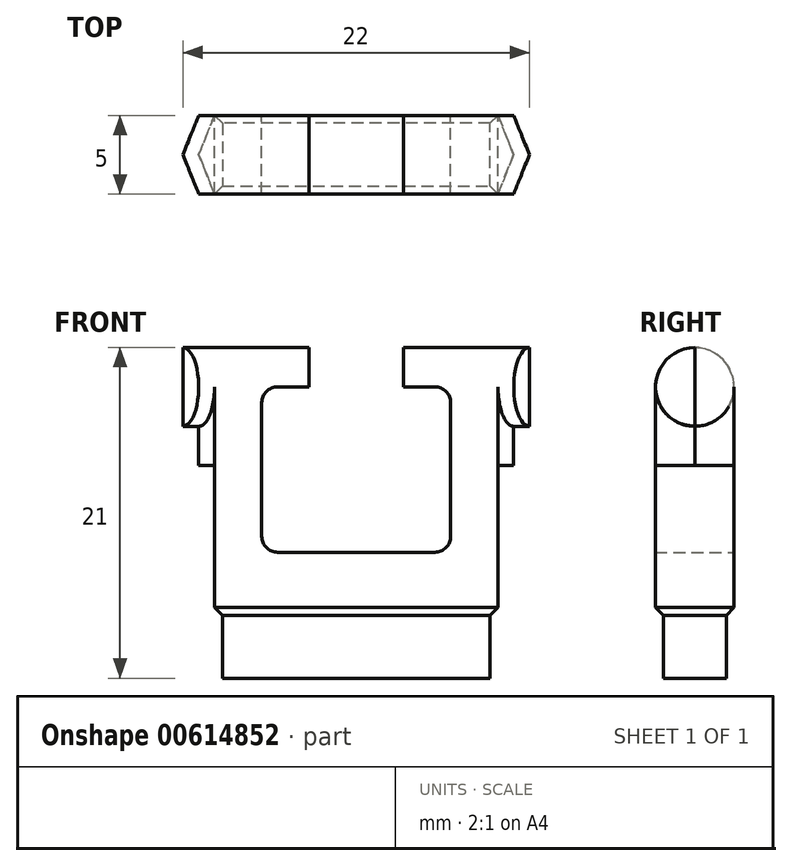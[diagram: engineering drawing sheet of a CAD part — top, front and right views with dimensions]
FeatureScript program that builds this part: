
annotation { "Feature Type Name" : "Feature", "Feature Type Description" : "" }
export const myFeature = defineFeature(function(context is Context, id is Id, definition is map)
    precondition{}
    {
        {
            var Q0;
            Q0=qCreatedBy(makeId("Front.planeOp"),FACE);
            var sketch = newSketch(context, id + "F0", { "sketchPlane" : qUnion([Q0])});
            skLineSegment(sketch, "E0", {"start": v(0, 0) * mm, "end": v(9, 0) * mm});
            skLineSegment(sketch, "E1", {"start": v(9, 0) * mm, "end": v(9, 14) * mm});
            skLineSegment(sketch, "E2", {"start": v(9, 14) * mm, "end": v(6, 14) * mm});
            skLineSegment(sketch, "E3", {"start": v(6, 14) * mm, "end": v(6, 3.5) * mm});
            skLineSegment(sketch, "E4", {"start": v(6, 3.5) * mm, "end": v(0, 3.5) * mm});
            skLineSegment(sketch, "E5", {"start": v(0, 3.5) * mm, "end": v(0, 0) * mm});
            skSolve(sketch);
        }
        {
            var Q0;
            Q0=qCreatedBy(makeId("Right.planeOp"),FACE);
            var sketch = newSketch(context, id + "F1", { "sketchPlane" : qUnion([Q0])});
            skCircle(sketch, "E6", {"center": v(0, 14) * mm, "radius": 2.5 * mm});
            skLineSegment(sketch, "E7", {"start": v(-2.5, 14) * mm, "end": v(2.5, 14) * mm});
            skSolve(sketch);
        }
        {
            var Q0;
            Q0=qSketchRegion(id+"F0",true);
            extrude(context, id + "F2", {"entities" : qUnion([Q0]), "endBound" : BoundingType.SYMMETRIC, "depth" : 5 * mm, "offsetDistance" : 25 * mm});
        }
        {
            var Q0;
            Q0=qSketchRegion(id+"F1",true);
            extrude(context, id + "F3", {"entities" : qUnion([Q0]), "operationType" : NewBodyOperationType.ADD, "depth" : 10 * mm, "offsetDistance" : 25 * mm});
        }
        {
            var Q0;
            Q0=qSketchRegion(id+"F1",true);
            extrude(context, id + "F4", {"entities" : qUnion([Q0]), "operationType" : NewBodyOperationType.REMOVE, "depth" : 3 * mm, "offsetDistance" : 25 * mm});
        }
        {
            var Q0;
            {var subQ0=sQuery(id+"F1.wireOp",EDGE,"E7");Q0=makeQuery(id+"F1.imprint","IMPRINT",FACE,{"disambiguationData":[TD([[makeQuery(id+"F1.imprint","IMPRINT",EDGE,{"derivedFrom":subQ0}),-1.0]])]});}
            extrude(context, id + "F5", {"entities" : qUnion([Q0]), "operationType" : NewBodyOperationType.REMOVE, "depth" : 6 * mm, "offsetDistance" : 25 * mm});
        }
        {
            var Q0;
            Q0=makeQuery(id+"F5.boolean.opBoolean","COPY",EDGE,{"derivedFrom":makeQuery(id+"F5.opExtrude","CAP_EDGE",EDGE,{"disambiguationData":[OSD([sQuery(id+"F1.wireOp",EDGE,"E7")])],"isStart":false})});
            var Q1;
            Q1=makeQuery(id+"F2.opExtrude","SWEPT_EDGE",EDGE,{"disambiguationData":[OSD([sQuery(id+"F0.wireOp",EDGE,"E3"),sQuery(id+"F0.wireOp",EDGE,"E4")])]});
            fillet(context, id + "F6", {"entities" : qUnion([Q0, Q1]), "radius" : 1 * mm, "tangentPropagation" : true, "allowEdgeOverflow" : false});
        }
        {
            var Q0;
            Q0=qCreatedBy(makeId("Top.planeOp"),FACE);
            var sketch = newSketch(context, id + "F7", { "sketchPlane" : qUnion([Q0])});
            skLineSegment(sketch, "E8", {"start": v(9, -2.5) * mm, "end": v(10, 0) * mm});
            skLineSegment(sketch, "E9", {"start": v(9, 2.5) * mm, "end": v(10, 0) * mm});
            skLineSegment(sketch, "E10", {"start": v(9, -2.5) * mm, "end": v(9, 2.5) * mm});
            skLineSegment(sketch, "E11", {"start": v(10, -2.5) * mm, "end": v(11, 0) * mm});
            skLineSegment(sketch, "E12", {"start": v(10, 2.5) * mm, "end": v(11, 0) * mm});
            skLineSegment(sketch, "E13", {"start": v(10, -2.5) * mm, "end": v(11.5, -2.5) * mm});
            skLineSegment(sketch, "E14", {"start": v(11.5, -2.5) * mm, "end": v(11.5, 2.5) * mm});
            skLineSegment(sketch, "E15", {"start": v(11.5, 2.5) * mm, "end": v(10, 2.5) * mm});
            skSolve(sketch);
        }
        {
            var Q0;
            Q0=makeQuery(id+"F7.imprint","IMPRINT",FACE,{"disambiguationData":[TD([[makeQuery(id+"F7.imprint","IMPRINT",EDGE,{"derivedFrom":sQuery(id+"F7.wireOp",EDGE,"E8")}),1.0]])]});
            extrude(context, id + "F8", {"entities" : qUnion([Q0]), "operationType" : NewBodyOperationType.ADD, "depth" : 14 * mm, "offsetDistance" : 25 * mm});
        }
        {
            var Q0;
            Q0=makeQuery(id+"F7.imprint","IMPRINT",FACE,{"disambiguationData":[TD([[makeQuery(id+"F7.imprint","IMPRINT",EDGE,{"derivedFrom":sQuery(id+"F7.wireOp",EDGE,"E8")}),1.0]])]});
            extrude(context, id + "F9", {"entities" : qUnion([Q0]), "operationType" : NewBodyOperationType.REMOVE, "depth" : 9 * mm, "offsetDistance" : 25 * mm});
        }
        {
            var Q0;
            Q0=makeQuery(id+"F3.opExtrude","CAP_FACE",FACE,{"disambiguationData":[OSD([sQuery(id+"F1.wireOp",EDGE,"E6")])],"isStart":false});
            extrude(context, id + "F10", {"entities" : qUnion([Q0]), "operationType" : NewBodyOperationType.ADD, "depth" : 1 * mm, "offsetDistance" : 25 * mm});
        }
        {
            var Q0;
            Q0=makeQuery(id+"F7.imprint","IMPRINT",FACE,{"disambiguationData":[TD([[makeQuery(id+"F7.imprint","IMPRINT",EDGE,{"derivedFrom":sQuery(id+"F7.wireOp",EDGE,"E11")}),-1.0]])]});
            extrude(context, id + "F11", {"entities" : qUnion([Q0]), "operationType" : NewBodyOperationType.REMOVE, "depth" : 16.5 * mm, "offsetDistance" : 25 * mm});
        }
        {
            var Q0;
            Q0=makeQuery(id+"F2.opExtrude","SWEPT_BODY",BODY,{"disambiguationData":[OSD([sQuery(id+"F0.wireOp",EDGE,"E0"),sQuery(id+"F0.wireOp",EDGE,"E1"),sQuery(id+"F0.wireOp",EDGE,"E2"),sQuery(id+"F0.wireOp",EDGE,"E3"),sQuery(id+"F0.wireOp",EDGE,"E4"),sQuery(id+"F0.wireOp",EDGE,"E5")])]});
            var Q1;
            Q1=makeQuery(id+"F2.opExtrude","SWEPT_FACE",FACE,{"disambiguationData":[OSD([sQuery(id+"F0.wireOp",EDGE,"E5")])]});
            mirror(context, id + "F12", {"operationType" : NewBodyOperationType.ADD, "entities" : qUnion([Q0]), "mirrorPlane" : qUnion([Q1])});
        }
        {
            var Q0;
            {var subQ0=makeQuery(id+"F8.boolean.opBoolean","MERGE",FACE,{"derivedFrom":[makeQuery(id+"F2.opExtrude","SWEPT_FACE",FACE,{"disambiguationData":[OSD([sQuery(id+"F0.wireOp",EDGE,"E0")])]}),makeQuery(id+"F8.opExtrude","CAP_FACE",FACE,{"disambiguationData":[OSD([sQuery(id+"F7.wireOp",EDGE,"E8"),sQuery(id+"F7.wireOp",EDGE,"E9"),sQuery(id+"F7.wireOp",EDGE,"E10")])],"isStart":true})]});Q0=makeQuery(id+"F12.boolean.opBoolean","MERGE",FACE,{"derivedFrom":[subQ0,makeQuery(id+"F12.opPattern","COPY",FACE,{"derivedFrom":subQ0,"instanceName":"1"})]});}
            extrude(context, id + "F13", {"entities" : qUnion([Q0]), "operationType" : NewBodyOperationType.ADD, "depth" : 0.5 * mm, "offsetDistance" : 25 * mm, "hasDraft" : true, "draftAngle" : 45 * degree, "draftPullDirection" : true});
        }
        {
            var Q0;
            Q0=makeQuery(id+"F13.opExtrude","CAP_FACE",FACE,{"disambiguationData":[OSD([sQuery(id+"F0.wireOp",EDGE,"E0"),sQuery(id+"F7.wireOp",EDGE,"E8"),sQuery(id+"F7.wireOp",EDGE,"E9"),sQuery(id+"F7.wireOp",EDGE,"E10")])],"isStart":false});
            extrude(context, id + "F14", {"entities" : qUnion([Q0]), "operationType" : NewBodyOperationType.ADD, "depth" : 4 * mm, "offsetDistance" : 25 * mm});
        }
    });
